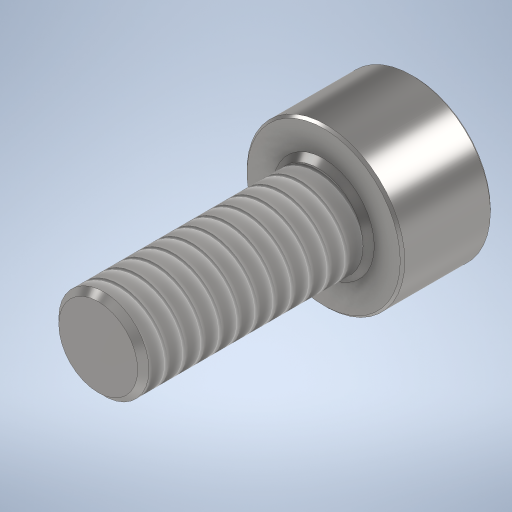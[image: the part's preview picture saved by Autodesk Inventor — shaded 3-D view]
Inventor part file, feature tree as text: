
AUTODESK INVENTOR PART (.ipt)
format: ipt  version: 2024 (Build 280153000, 153)  size: 330,240 bytes
history: native  units: mm
features: extrude x3, chamfer x3, sketch x2, thread x1, hole x1
ambient origin geometry x8: Origin, YZ Plane, XZ Plane, XY Plane, X Axis, Y Axis, Z Axis, Center Point
bodies: Solid1 (feature_tree)
feature tree (10):
  sketch  "Sketch1"  dims[d0=7.0mm d1=4.0mm]
  extrude  "Extrusion1"  Depth=4.0mm
  extrude  "Extrusion2"  Depth=2.0mm TaperAngle=0.0deg
  thread  "Thread1"  [1 undecoded]
  chamfer  "Chamfer1"  Distance=2.0mm Angle=45.0deg
  sketch  "Sketch2"  dims[d2=10.0mm d3=0.0mm d4=4.0mm d5=0.0mm d6=15.0mm d7=0.0mm d8=0.1mm d9=2.0mm d10=45.0deg d11=2.75mm d12=3.0mm d15=0.4mm d16=2.0mm d17=45.0deg d18=3.0mm d19=0.0mm d20=0.25mm d21=2.0mm d22=45.0deg d23=2.75mm d24=6.0mm d25=4.0mm d26=2.0mm d27=90.0deg d28=2.0mm d29=150.0deg]
  hole  "Hole1"  [1 undecoded]
  chamfer  "Chamfer2"  Distance=3.0mm
  extrude  "Extrusion4"  Depth=2.0mm TaperAngle=45.0deg
  chamfer  "Chamfer3"  Distance=3.0mm
note: 2 required parameter values undecoded (feature->parameter linkage not recoverable at this tier; creation-order binding heuristic only, values carry confidence <= 0.55)
